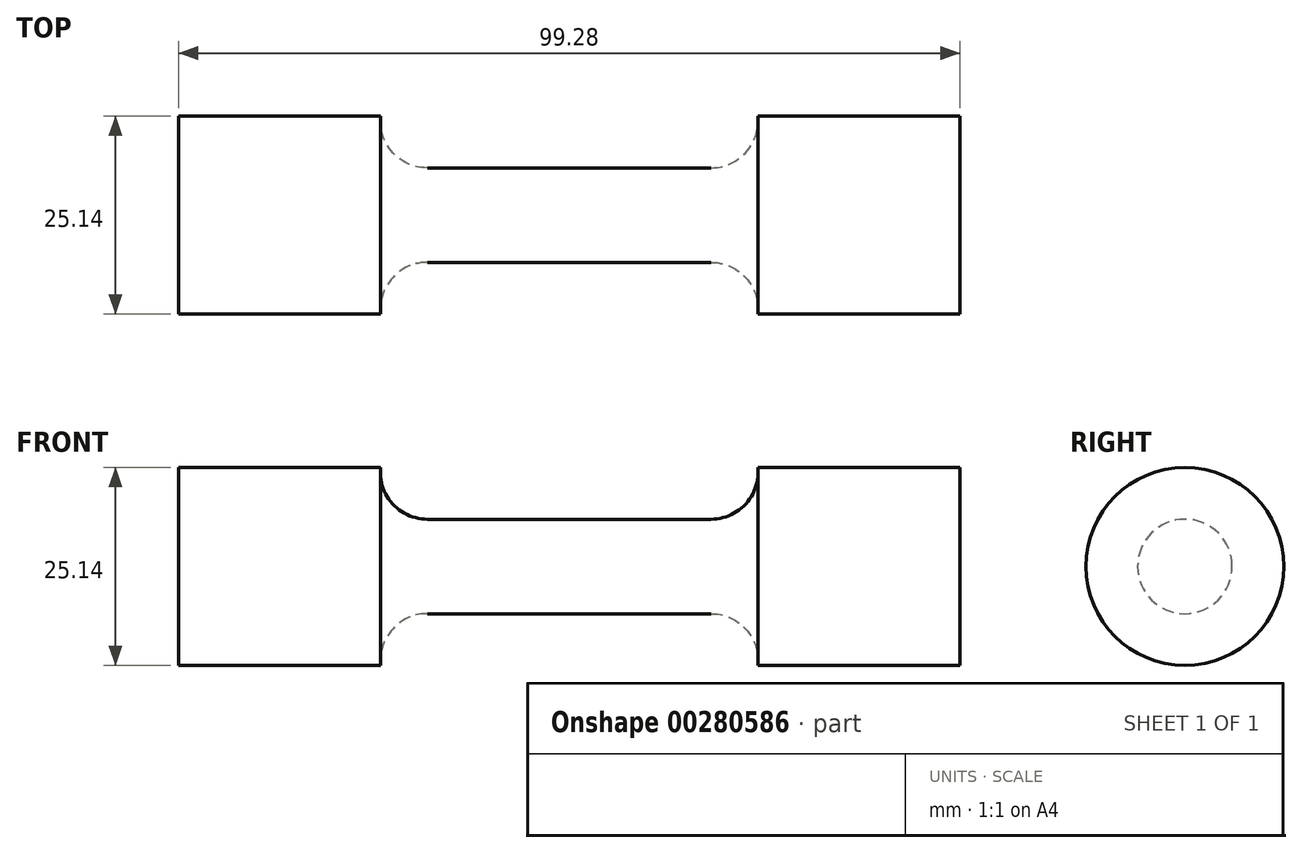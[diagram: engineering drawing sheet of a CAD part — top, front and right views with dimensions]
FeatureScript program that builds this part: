
annotation { "Feature Type Name" : "Feature", "Feature Type Description" : "" }
export const myFeature = defineFeature(function(context is Context, id is Id, definition is map)
    precondition{}
    {
        {
            var Q0;
            Q0=qCreatedBy(makeId("Front.planeOp"),FACE);
            var sketch = newSketch(context, id + "F0", { "sketchPlane" : qUnion([Q0])});
            skLineSegment(sketch, "E0", {"start": v(0, 6) * mm, "end": v(18, 6) * mm});
            skArc(sketch, "E1", {"start": v(18, 6) * mm, "mid": v(22.44, 7.96) * mm, "end": v(23.97, 12.57) * mm});
            skLineSegment(sketch, "E2", {"start": v(23.97, 12.57) * mm, "end": v(49.64, 12.57) * mm});
            skLineSegment(sketch, "E3", {"start": v(49.64, 12.57) * mm, "end": v(49.64, 0) * mm});
            skLineSegment(sketch, "E4.MirrorCS", {"start": v(0, 6) * mm, "end": v(-18, 6) * mm});
            skLineSegment(sketch, "E5.MirrorCS", {"start": v(-49.64, 12.57) * mm, "end": v(-49.64, 0) * mm});
            skLineSegment(sketch, "E6.MirrorCS", {"start": v(-23.97, 12.57) * mm, "end": v(-49.64, 12.57) * mm});
            skArc(sketch, "E7.MirrorCS", {"start": v(-18, 6) * mm, "mid": v(-22.44, 7.96) * mm, "end": v(-23.97, 12.57) * mm});
            skLineSegment(sketch, "E8", {"start": v(-49.64, 0) * mm, "end": v(49.64, 0) * mm});
            skSolve(sketch);
        }
        {
            var Q0;
            Q0 = qSketchRegion(id + "F0", true);
            var Q1;
            Q1=sQuery(id+"F0.wireOp",EDGE,"E8");
            revolve(context, id + "F1", {"entities" : qUnion([Q0]), "axis" : qUnion([Q1]), "revolveType" : RevolveType.FULL});
        }
    });
